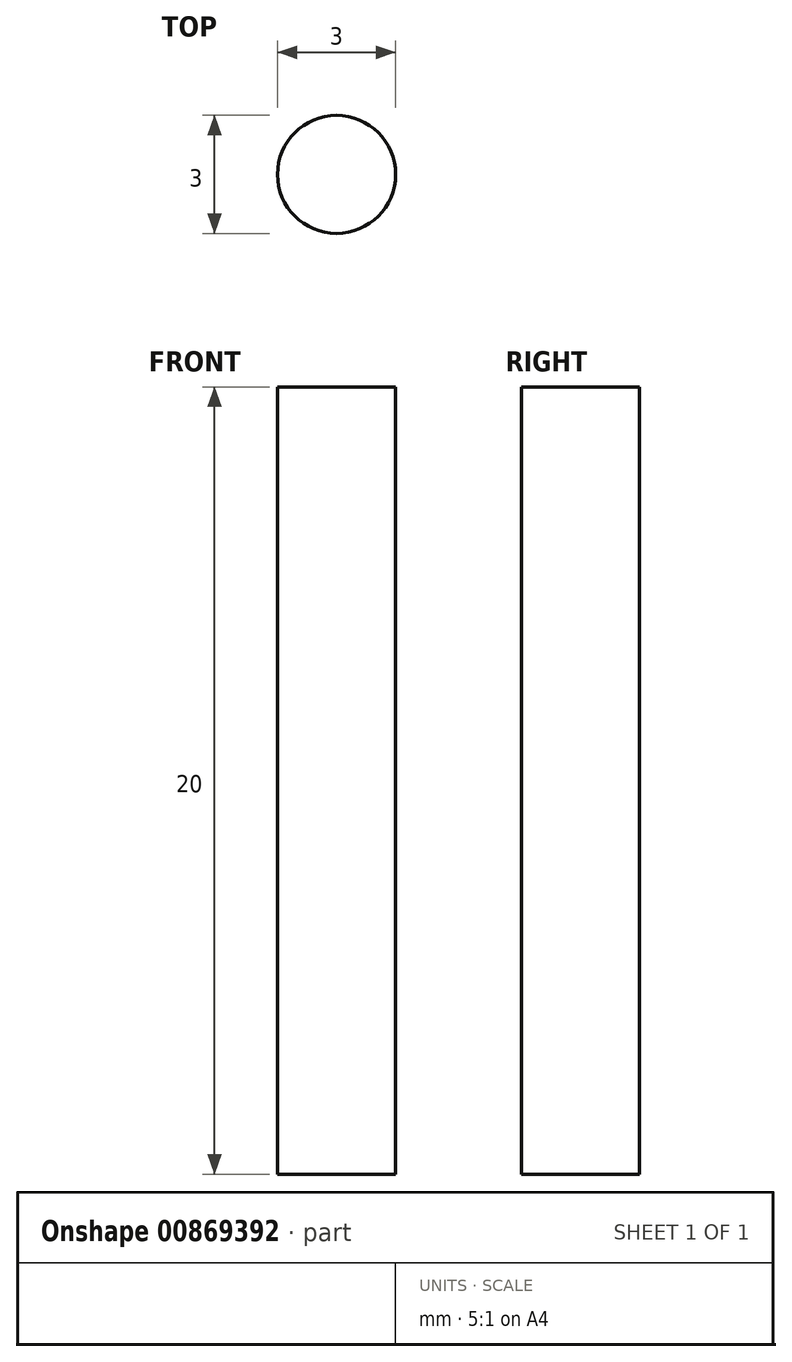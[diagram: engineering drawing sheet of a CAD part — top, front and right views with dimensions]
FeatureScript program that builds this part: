
annotation { "Feature Type Name" : "Feature", "Feature Type Description" : "" }
export const myFeature = defineFeature(function(context is Context, id is Id, definition is map)
    precondition{}
    {
        {
            var Q0;
            Q0=qCreatedBy(makeId("Top.planeOp"),FACE);
            var sketch = newSketch(context, id + "F0", { "sketchPlane" : qUnion([Q0])});
            skCircle(sketch, "E0", {"center": v(0, 0) * mm, "radius": 1.5 * mm});
            skSolve(sketch);
        }
        {
            var Q0;
            Q0 = qSketchRegion(id + "F0", true);
            extrude(context, id + "F1", {"entities" : qUnion([Q0]), "depth" : 20 * mm, "offsetDistance" : 25 * mm});
        }
    });
